# Revit family: Контроллер видеостены STS-355-L_RV17_LOD400
name_source: partatom
category: Электрооборудование
revit_build: Autodesk Revit 2017 (Build: 20170118_1100(x64)
units: mm (PartAtom-declared; Revit-internal decimal feet)

## family parameters
Всегда вертикально = Нет
Конфигурация панели = Два столбца, слева направо
На основе рабочей плоскости = Нет
Общий = Нет
При загрузке вырезать с полостями = Нет
Размер круглого соединителя = Использовать диаметр
Тип детали = Щит
Точка расчета площади = Нет

## types (1)
- Контроллер видеостены STS-355-L
    ADSK_URL документации изделия = https://stilsoft.ru
    ADSK_Единица измерения = шт.
    ADSK_Завод-изготовитель = ООО «Основа Безопасности»
    ADSK_Количество = 1
    ADSK_Марка = СТВФ.426484.057
    ADSK_Масса = 2.65
    ADSK_Наименование = Контроллер видеостены STS-355-L
    ADSK_Размер_Высота = 90 мм
    ADSK_Размер_Длина = 234 мм
    ADSK_Размер_Ширина = 222 мм
    Ethernet = 1x1000 Мбит/с
    Диапазон рабочих температур, °С = от +5 до +50
    Количество отображаемых видеоканалов на двух мониторах, до, шт. = 48
    Количество отображаемых видеоканалов на одном мониторе, до, шт. = 32
    Количество подключаемых мониторов, до, шт = 2
    Мощность = 95
    Напряжение = 220
    Объем накопителя, ГБ = 500
    Оперативная память, Гб = 8
    Установленное ПО = ОС «Astra Linux Common Edition», Антивирус Касперского, Базовое серверное ПО «Синергет»
